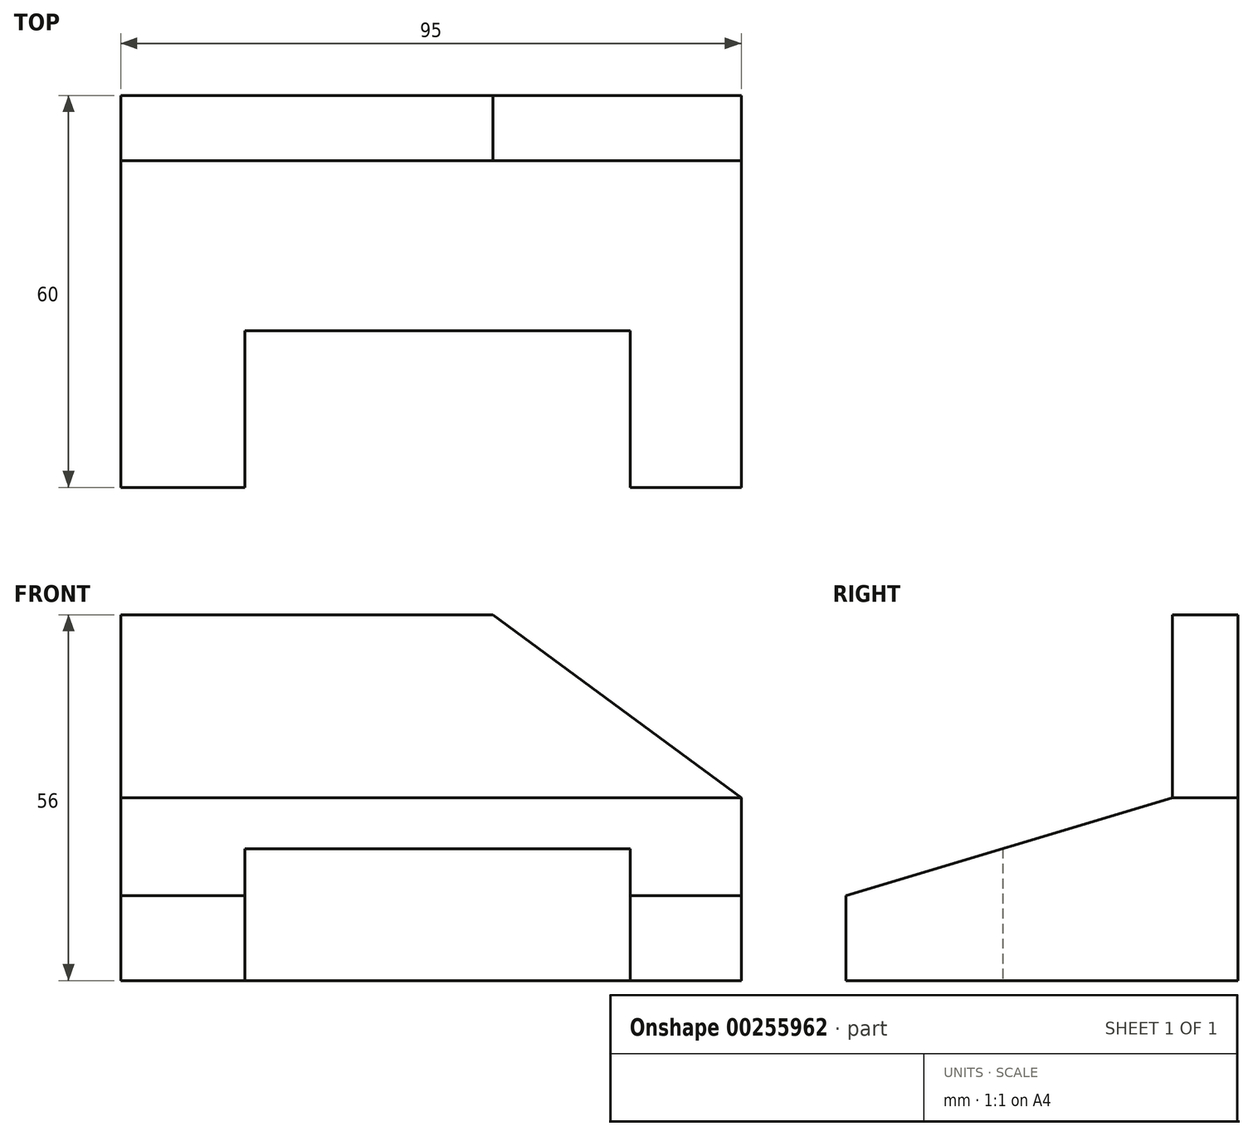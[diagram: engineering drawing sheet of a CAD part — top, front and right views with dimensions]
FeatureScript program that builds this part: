
annotation { "Feature Type Name" : "Feature", "Feature Type Description" : "" }
export const myFeature = defineFeature(function(context is Context, id is Id, definition is map)
    precondition{}
    {
        {
            var Q0;
            Q0=qCreatedBy(makeId("Right.planeOp"),FACE);
            var sketch = newSketch(context, id + "F0", { "sketchPlane" : qUnion([Q0])});
            skLineSegment(sketch, "E0", {"start": v(0, 0) * mm, "end": v(0, 56) * mm});
            skLineSegment(sketch, "E1", {"start": v(0, 56) * mm, "end": v(-10, 56) * mm});
            skLineSegment(sketch, "E2", {"start": v(-10, 56) * mm, "end": v(-10, 28) * mm});
            skLineSegment(sketch, "E3", {"start": v(-10, 28) * mm, "end": v(-60, 13) * mm});
            skLineSegment(sketch, "E4", {"start": v(-60, 13) * mm, "end": v(-60, 0) * mm});
            skLineSegment(sketch, "E5", {"start": v(-60, 0) * mm, "end": v(0, 0) * mm});
            skSolve(sketch);
        }
        {
            var Q0;
            Q0=qSketchRegion(id+"F0",true);
            extrude(context, id + "F1", {"entities" : qUnion([Q0]), "depth" : 95 * mm});
        }
        {
            var Q0;
            Q0=makeQuery(id+"F1.opExtrude","SWEPT_FACE",FACE,{"disambiguationData":[OSD([sQuery(id+"F0.wireOp",EDGE,"E2")])]});
            var sketch = newSketch(context, id + "F2", { "sketchPlane" : qUnion([Q0])});
            skLineSegment(sketch, "E6", {"start": v(57, 56) * mm, "end": v(95, 28) * mm});
            skSolve(sketch);
        }
        {
            var Q0;
            {var subQ0=sQuery(id+"F2.wireOp",EDGE,"E6");Q0=makeQuery(id+"F2.imprint","IMPRINT",FACE,{"disambiguationData":[TD([[makeQuery(id+"F2.imprint","IMPRINT",EDGE,{"derivedFrom":subQ0}),1.0]])]});}
            var Q1;
            Q1=makeQuery(id+"F1.opExtrude","SWEPT_FACE",FACE,{"disambiguationData":[OSD([sQuery(id+"F0.wireOp",EDGE,"E0")])]});
            var Q2;
            Q2=makeQuery(id+"F1.opExtrude","SWEPT_BODY",BODY,{"disambiguationData":[OSD([sQuery(id+"F0.wireOp",EDGE,"E0"),sQuery(id+"F0.wireOp",EDGE,"E1"),sQuery(id+"F0.wireOp",EDGE,"E2"),sQuery(id+"F0.wireOp",EDGE,"E3"),sQuery(id+"F0.wireOp",EDGE,"E4"),sQuery(id+"F0.wireOp",EDGE,"E5")])]});
            var Q3;
            Q3=makeQuery(id+"F1.opExtrude","CAP_VERTEX",VERTEX,{"disambiguationData":[OSD([sQuery(id+"F0.wireOp",EDGE,"E0"),sQuery(id+"F0.wireOp",EDGE,"E5")])],"isStart":false});
            extrude(context, id + "F3", {"entities" : qUnion([Q0]), "operationType" : NewBodyOperationType.REMOVE, "endBound" : BoundingType.THROUGH_ALL, "oppositeDirection" : true, "endBoundEntityFace" : qUnion([Q1]), "endBoundEntityBody" : qUnion([Q2]), "endBoundEntityVertex" : qUnion([Q3]), "depth" : 25 * mm});
        }
        {
            var Q0;
            Q0=makeQuery(id+"F1.opExtrude","SWEPT_FACE",FACE,{"disambiguationData":[OSD([sQuery(id+"F0.wireOp",EDGE,"E5")])]});
            var sketch = newSketch(context, id + "F4", { "sketchPlane" : qUnion([Q0])});
            skLineSegment(sketch, "E7.bottom", {"start": v(78, 60) * mm, "end": v(19, 60) * mm});
            skLineSegment(sketch, "E7.top", {"start": v(78, 36) * mm, "end": v(19, 36) * mm});
            skLineSegment(sketch, "E7.left", {"start": v(78, 60) * mm, "end": v(78, 36) * mm});
            skLineSegment(sketch, "E7.right", {"start": v(19, 60) * mm, "end": v(19, 36) * mm});
            skSolve(sketch);
        }
        {
            var Q0;
            Q0=makeQuery(id+"F4.imprint","IMPRINT",FACE,{"disambiguationData":[TD([[makeQuery(id+"F4.imprint","IMPRINT",EDGE,{"derivedFrom":sQuery(id+"F4.wireOp",EDGE,"E7.bottom")}),1.0]])]});
            extrude(context, id + "F5", {"entities" : qUnion([Q0]), "operationType" : NewBodyOperationType.REMOVE, "endBound" : BoundingType.THROUGH_ALL, "oppositeDirection" : true, "depth" : 25 * mm});
        }
    });
